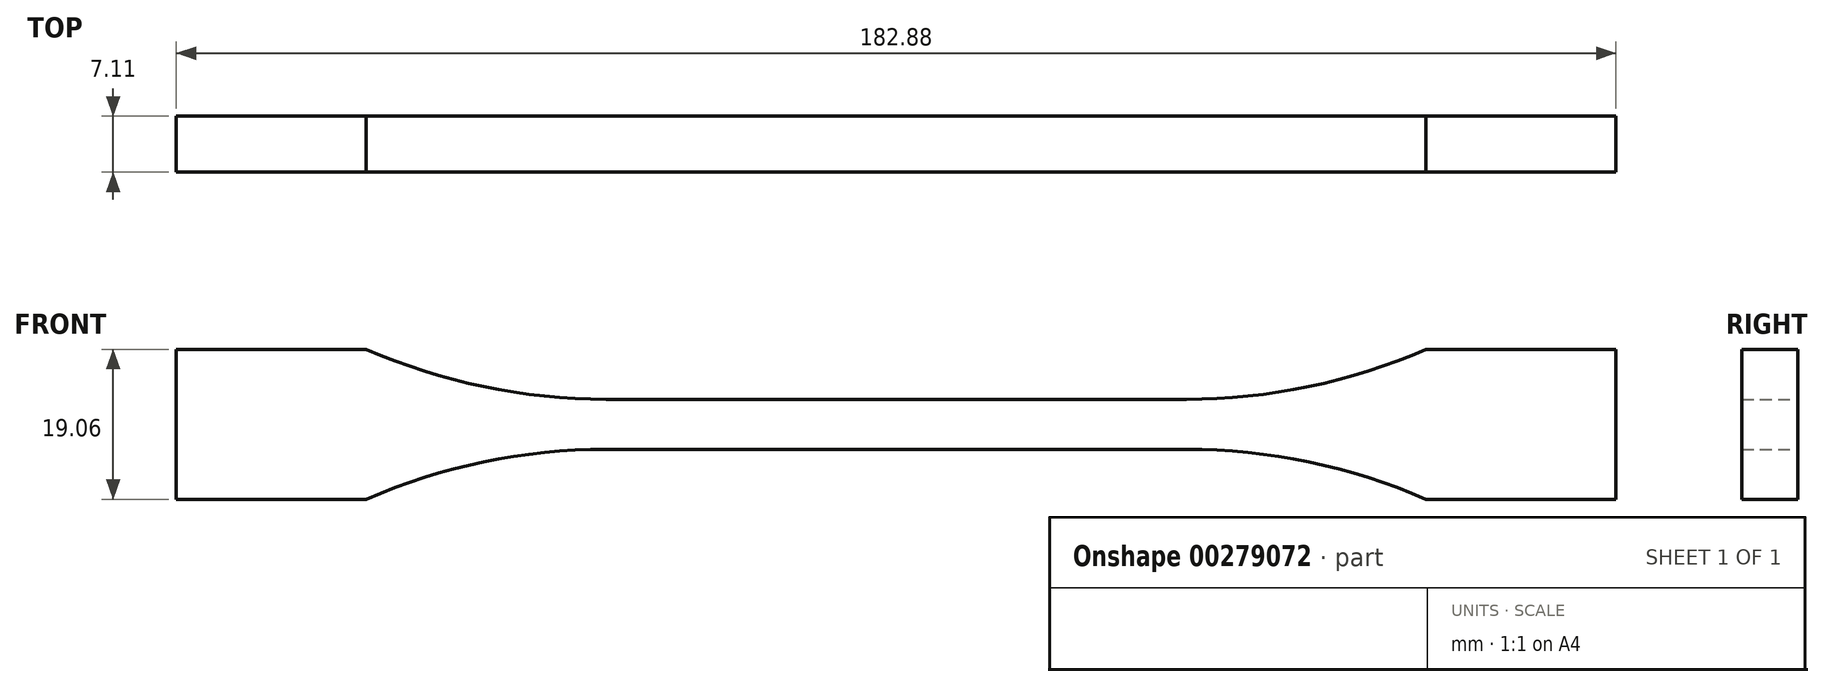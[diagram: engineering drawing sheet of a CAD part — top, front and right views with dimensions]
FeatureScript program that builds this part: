
annotation { "Feature Type Name" : "Feature", "Feature Type Description" : "" }
export const myFeature = defineFeature(function(context is Context, id is Id, definition is map)
    precondition{}
    {
        {
            var Q0;
            Q0=qCreatedBy(makeId("Front.planeOp"),FACE);
            var sketch = newSketch(context, id + "F0", { "sketchPlane" : qUnion([Q0])});
            skLineSegment(sketch, "E0", {"start": v(0, 3.17) * mm, "end": v(36.86, 3.17) * mm});
            skArc(sketch, "E1", {"start": v(36.86, 3.17) * mm, "mid": v(52.41, 4.78) * mm, "end": v(67.31, 9.53) * mm});
            skLineSegment(sketch, "E2", {"start": v(67.31, 9.52) * mm, "end": v(91.44, 9.52) * mm});
            skLineSegment(sketch, "E3", {"start": v(91.44, 9.53) * mm, "end": v(91.44, 0) * mm});
            skLineSegment(sketch, "E4.MirrorCS", {"start": v(67.31, -9.53) * mm, "end": v(91.44, -9.53) * mm});
            skLineSegment(sketch, "E5.MirrorCS", {"start": v(91.44, -9.53) * mm, "end": v(91.44, 0) * mm});
            skLineSegment(sketch, "E6.MirrorCS", {"start": v(0, -3.18) * mm, "end": v(36.86, -3.18) * mm});
            skArc(sketch, "E7.MirrorCS", {"start": v(36.86, -3.17) * mm, "mid": v(52.41, -4.78) * mm, "end": v(67.31, -9.53) * mm});
            skArc(sketch, "E8.MirrorCS", {"start": v(-36.86, -3.17) * mm, "mid": v(-52.41, -4.78) * mm, "end": v(-67.31, -9.53) * mm});
            skLineSegment(sketch, "E9.MirrorCS", {"start": v(0, -3.18) * mm, "end": v(-36.86, -3.18) * mm});
            skArc(sketch, "E10.MirrorCS", {"start": v(-36.86, 3.17) * mm, "mid": v(-52.41, 4.78) * mm, "end": v(-67.31, 9.53) * mm});
            skLineSegment(sketch, "E11.MirrorCS", {"start": v(-67.31, 9.53) * mm, "end": v(-91.44, 9.52) * mm});
            skLineSegment(sketch, "E12.MirrorCS", {"start": v(-67.31, -9.53) * mm, "end": v(-91.44, -9.53) * mm});
            skLineSegment(sketch, "E13.MirrorCS", {"start": v(-91.44, -9.53) * mm, "end": v(-91.44, 0) * mm});
            skLineSegment(sketch, "E14.MirrorCS", {"start": v(0, 3.18) * mm, "end": v(-36.86, 3.17) * mm});
            skLineSegment(sketch, "E15.MirrorCS", {"start": v(-91.44, 9.53) * mm, "end": v(-91.44, 0) * mm});
            skSolve(sketch);
        }
        {
            var Q0;
            Q0 = qSketchRegion(id + "F0", true);
            extrude(context, id + "F1", {"entities" : qUnion([Q0]), "depth" : 7.11 * mm});
        }
    });
